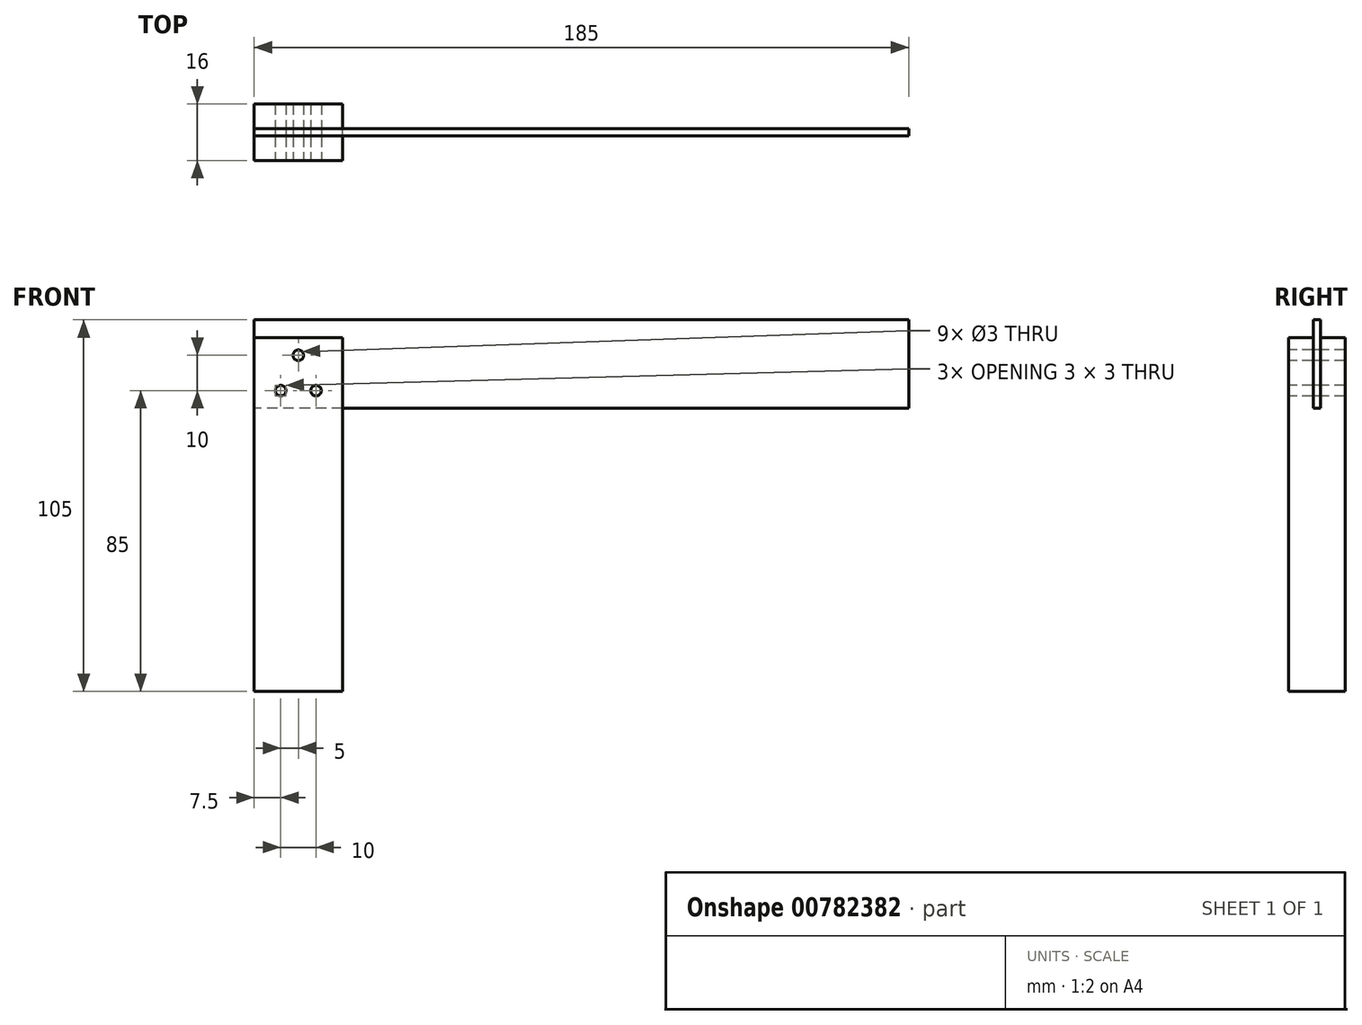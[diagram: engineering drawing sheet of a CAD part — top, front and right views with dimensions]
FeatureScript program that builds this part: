
annotation { "Feature Type Name" : "Feature", "Feature Type Description" : "" }
export const myFeature = defineFeature(function(context is Context, id is Id, definition is map)
    precondition{}
    {
        {
            var Q0;
            Q0=qCreatedBy(makeId("Front.planeOp"),FACE);
            var sketch = newSketch(context, id + "F0", { "sketchPlane" : qUnion([Q0])});
            skLineSegment(sketch, "E0.bottom", {"start": v(0, 0) * mm, "end": v(-25, 0) * mm});
            skLineSegment(sketch, "E0.top", {"start": v(0, 100) * mm, "end": v(-25, 100) * mm});
            skLineSegment(sketch, "E0.left", {"start": v(0, 0) * mm, "end": v(0, 100) * mm});
            skLineSegment(sketch, "E0.right", {"start": v(-25, 0) * mm, "end": v(-25, 100) * mm});
            skSolve(sketch);
        }
        {
            var Q0;
            Q0=makeQuery(id+"F0.imprint","IMPRINT",FACE,{"disambiguationData":[TD([[makeQuery(id+"F0.imprint","IMPRINT",EDGE,{"derivedFrom":sQuery(id+"F0.wireOp",EDGE,"E0.bottom")}),-1.0]])]});
            extrude(context, id + "F1", {"entities" : qUnion([Q0]), "depth" : 16 * mm, "offsetDistance" : 25 * mm});
        }
        {
            var Q0;
            Q0=makeQuery(id+"F1.opExtrude","SWEPT_FACE",FACE,{"disambiguationData":[OSD([sQuery(id+"F0.wireOp",EDGE,"E0.right")])]});
            var sketch = newSketch(context, id + "F2", { "sketchPlane" : qUnion([Q0])});
            skLineSegment(sketch, "E1.bottom", {"start": v(7, 100) * mm, "end": v(9, 100) * mm});
            skLineSegment(sketch, "E1.top", {"start": v(7, 80) * mm, "end": v(9, 80) * mm});
            skLineSegment(sketch, "E1.left", {"start": v(7, 100) * mm, "end": v(7, 80) * mm});
            skLineSegment(sketch, "E1.right", {"start": v(9, 100) * mm, "end": v(9, 80) * mm});
            skSolve(sketch);
        }
        {
            var Q0;
            Q0=makeQuery(id+"F2.imprint","IMPRINT",FACE,{"disambiguationData":[TD([[makeQuery(id+"F2.imprint","IMPRINT",EDGE,{"derivedFrom":sQuery(id+"F2.wireOp",EDGE,"E1.bottom")}),1.0]])]});
            var Q1;
            Q1=makeQuery(id+"F1.opExtrude","SWEPT_FACE",FACE,{"disambiguationData":[OSD([sQuery(id+"F0.wireOp",EDGE,"E0.left")])]});
            extrude(context, id + "F3", {"entities" : qUnion([Q0]), "operationType" : NewBodyOperationType.REMOVE, "endBound" : BoundingType.UP_TO_SURFACE, "oppositeDirection" : true, "depth" : 25 * mm, "endBoundEntityFace" : qUnion([Q1]), "offsetDistance" : 25 * mm});
        }
        {
            var Q0;
            Q0=makeQuery(id+"F1.opExtrude","SWEPT_FACE",FACE,{"disambiguationData":[OSD([sQuery(id+"F0.wireOp",EDGE,"E0.right")])]});
            var sketch = newSketch(context, id + "F4", { "sketchPlane" : qUnion([Q0])});
            skLineSegment(sketch, "E2.bottom", {"start": v(7, 80) * mm, "end": v(9, 80) * mm});
            skLineSegment(sketch, "E2.top", {"start": v(7, 105) * mm, "end": v(9, 105) * mm});
            skLineSegment(sketch, "E2.left", {"start": v(7, 80) * mm, "end": v(7, 105) * mm});
            skLineSegment(sketch, "E2.right", {"start": v(9, 80) * mm, "end": v(9, 105) * mm});
            skSolve(sketch);
        }
        {
            var Q0;
            {var subQ10=sQuery(id+"F4.wireOp",EDGE,"E2.bottom");Q0=makeQuery(id+"F4.imprint","IMPRINT",FACE,{"disambiguationData":[TD([[makeQuery(id+"F4.imprint","IMPRINT",EDGE,{"derivedFrom":subQ10}),1.0]])]});}
            extrude(context, id + "F5", {"entities" : qUnion([Q0]), "oppositeDirection" : true, "depth" : 185 * mm, "offsetDistance" : 25 * mm});
        }
        {
            var Q0;
            Q0=makeQuery(id+"F1.opExtrude","CAP_FACE",FACE,{"disambiguationData":[OSD([sQuery(id+"F0.wireOp",EDGE,"E0.bottom"),sQuery(id+"F0.wireOp",EDGE,"E0.top"),sQuery(id+"F0.wireOp",EDGE,"E0.left"),sQuery(id+"F0.wireOp",EDGE,"E0.right")])],"isStart":false});
            var sketch = newSketch(context, id + "F6", { "sketchPlane" : qUnion([Q0])});
            skCircle(sketch, "E3", {"center": v(-7.5, 85) * mm, "radius": 1.5 * mm});
            skCircle(sketch, "E4", {"center": v(-12.5, 95) * mm, "radius": 1.5 * mm});
            skCircle(sketch, "E5", {"center": v(-17.5, 85) * mm, "radius": 1.5 * mm});
            skSolve(sketch);
        }
        {
            var Q0;
            Q0 = qSketchRegion(id + "F6", true);
            var Q1;
            Q1=makeQuery(id+"F1.opExtrude","CAP_FACE",FACE,{"disambiguationData":[OSD([sQuery(id+"F0.wireOp",EDGE,"E0.bottom"),sQuery(id+"F0.wireOp",EDGE,"E0.top"),sQuery(id+"F0.wireOp",EDGE,"E0.left"),sQuery(id+"F0.wireOp",EDGE,"E0.right")])],"isStart":true});
            extrude(context, id + "F7", {"entities" : qUnion([Q0]), "operationType" : NewBodyOperationType.REMOVE, "endBound" : BoundingType.UP_TO_SURFACE, "oppositeDirection" : true, "depth" : 25 * mm, "endBoundEntityFace" : qUnion([Q1]), "offsetDistance" : 25 * mm});
        }
        {
            var Q0;
            Q0=makeQuery(id+"F1.opExtrude","CAP_FACE",FACE,{"disambiguationData":[OSD([sQuery(id+"F0.wireOp",EDGE,"E0.bottom"),sQuery(id+"F0.wireOp",EDGE,"E0.top"),sQuery(id+"F0.wireOp",EDGE,"E0.left"),sQuery(id+"F0.wireOp",EDGE,"E0.right")])],"isStart":false});
            var sketch = newSketch(context, id + "F8", { "sketchPlane" : qUnion([Q0])});
            skCircle(sketch, "E6", {"center": v(-12.5, 95) * mm, "radius": 1.5 * mm});
            skSolve(sketch);
        }
        {
            var Q0;
            Q0 = qSketchRegion(id + "F8", true);
            var Q1;
            Q1=makeQuery(id+"F1.opExtrude","CAP_FACE",FACE,{"disambiguationData":[OSD([sQuery(id+"F0.wireOp",EDGE,"E0.bottom"),sQuery(id+"F0.wireOp",EDGE,"E0.top"),sQuery(id+"F0.wireOp",EDGE,"E0.left"),sQuery(id+"F0.wireOp",EDGE,"E0.right")])],"isStart":true});
            extrude(context, id + "F9", {"entities" : qUnion([Q0]), "endBound" : BoundingType.UP_TO_SURFACE, "oppositeDirection" : true, "depth" : 25 * mm, "endBoundEntityFace" : qUnion([Q1]), "offsetDistance" : 25 * mm});
        }
        {
            var Q0;
            Q0=makeQuery(id+"F1.opExtrude","CAP_FACE",FACE,{"disambiguationData":[OSD([sQuery(id+"F0.wireOp",EDGE,"E0.bottom"),sQuery(id+"F0.wireOp",EDGE,"E0.top"),sQuery(id+"F0.wireOp",EDGE,"E0.left"),sQuery(id+"F0.wireOp",EDGE,"E0.right")])],"isStart":false});
            var sketch = newSketch(context, id + "F10", { "sketchPlane" : qUnion([Q0])});
            skCircle(sketch, "E7", {"center": v(-17.5, 85) * mm, "radius": 1.5 * mm});
            skSolve(sketch);
        }
        {
            var Q0;
            Q0 = qSketchRegion(id + "F10", true);
            var Q1;
            Q1=makeQuery(id+"F1.opExtrude","CAP_FACE",FACE,{"disambiguationData":[OSD([sQuery(id+"F0.wireOp",EDGE,"E0.bottom"),sQuery(id+"F0.wireOp",EDGE,"E0.top"),sQuery(id+"F0.wireOp",EDGE,"E0.left"),sQuery(id+"F0.wireOp",EDGE,"E0.right")])],"isStart":true});
            extrude(context, id + "F11", {"entities" : qUnion([Q0]), "endBound" : BoundingType.UP_TO_SURFACE, "oppositeDirection" : true, "depth" : 25 * mm, "endBoundEntityFace" : qUnion([Q1]), "offsetDistance" : 25 * mm});
        }
        {
            var Q0;
            Q0=makeQuery(id+"F1.opExtrude","CAP_FACE",FACE,{"disambiguationData":[OSD([sQuery(id+"F0.wireOp",EDGE,"E0.bottom"),sQuery(id+"F0.wireOp",EDGE,"E0.top"),sQuery(id+"F0.wireOp",EDGE,"E0.left"),sQuery(id+"F0.wireOp",EDGE,"E0.right")])],"isStart":false});
            var sketch = newSketch(context, id + "F12", { "sketchPlane" : qUnion([Q0])});
            skCircle(sketch, "E8", {"center": v(-7.5, 85) * mm, "radius": 1.5 * mm});
            skSolve(sketch);
        }
        {
            var Q0;
            Q0 = qSketchRegion(id + "F12", true);
            var Q1;
            Q1=makeQuery(id+"F1.opExtrude","CAP_FACE",FACE,{"disambiguationData":[OSD([sQuery(id+"F0.wireOp",EDGE,"E0.bottom"),sQuery(id+"F0.wireOp",EDGE,"E0.top"),sQuery(id+"F0.wireOp",EDGE,"E0.left"),sQuery(id+"F0.wireOp",EDGE,"E0.right")])],"isStart":true});
            extrude(context, id + "F13", {"entities" : qUnion([Q0]), "endBound" : BoundingType.UP_TO_SURFACE, "oppositeDirection" : true, "depth" : 25 * mm, "endBoundEntityFace" : qUnion([Q1]), "offsetDistance" : 25 * mm});
        }
    });
